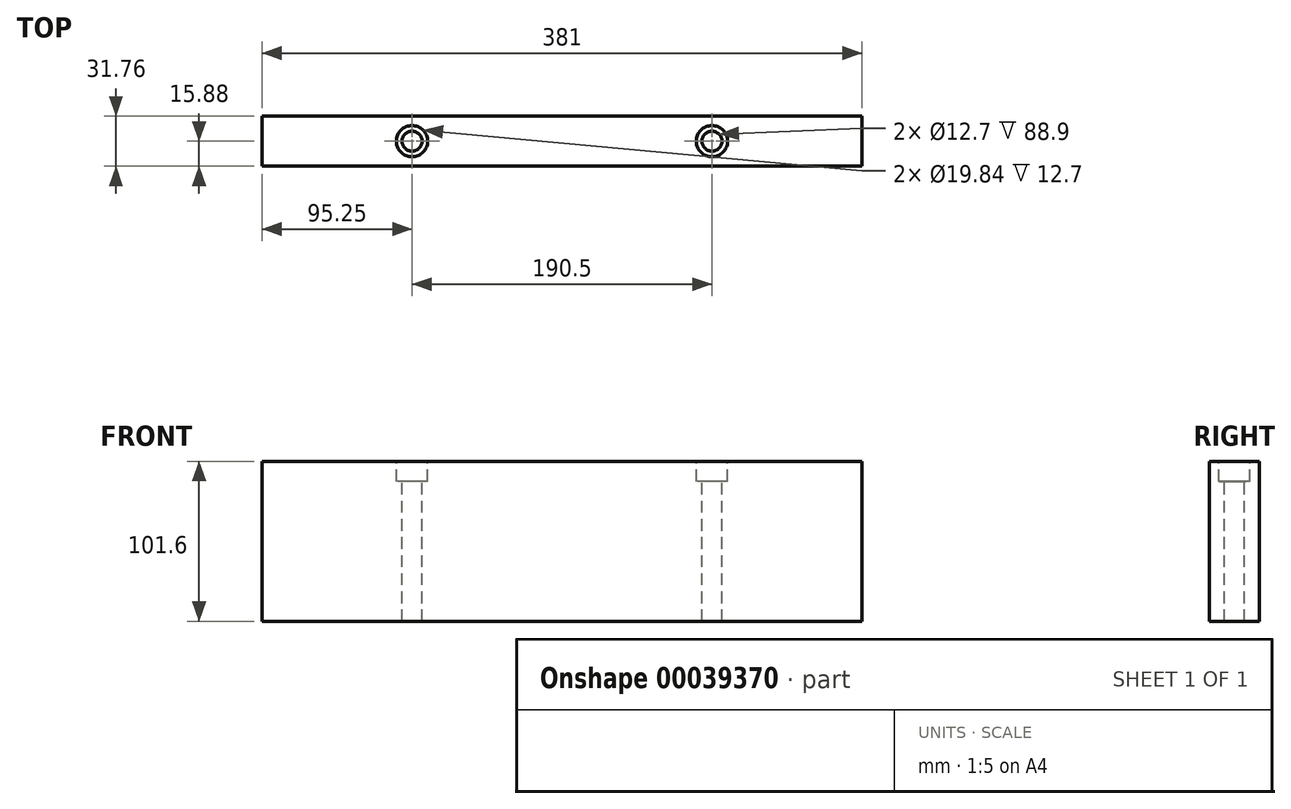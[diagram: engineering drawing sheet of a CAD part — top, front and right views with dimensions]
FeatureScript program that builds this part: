
annotation { "Feature Type Name" : "Feature", "Feature Type Description" : "" }
export const myFeature = defineFeature(function(context is Context, id is Id, definition is map)
    precondition{}
    {
        {
            var Q0;
            Q0=qCreatedBy(makeId("Top.planeOp"),FACE);
            var sketch = newSketch(context, id + "F0", { "sketchPlane" : qUnion([Q0])});
            skLineSegment(sketch, "E0", {"start": v(0, 247.96) * mm, "end": v(0, -242.63) * mm});
            skLineSegment(sketch, "E1", {"start": v(-246.65, 0) * mm, "end": v(251.52, 0) * mm});
            skLineSegment(sketch, "E2.bottom", {"start": v(-190.5, 15.88) * mm, "end": v(190.5, 15.88) * mm});
            skLineSegment(sketch, "E2.top", {"start": v(-190.5, -15.88) * mm, "end": v(190.5, -15.88) * mm});
            skLineSegment(sketch, "E2.left", {"start": v(-190.5, 15.88) * mm, "end": v(-190.5, -15.88) * mm});
            skLineSegment(sketch, "E2.right", {"start": v(190.5, 15.87) * mm, "end": v(190.5, -15.87) * mm});
            skSolve(sketch);
        }
        {
            var Q0;
            Q0 = qSketchRegion(id + "F0", true);
            extrude(context, id + "F1", {"entities" : qUnion([Q0]), "depth" : 101.6 * mm});
        }
        {
            var Q0;
            Q0=makeQuery(id+"F1.opExtrude","CAP_FACE",FACE,{"disambiguationData":[OSD([sQuery(id+"F0.wireOp",EDGE,"E2.bottom"),sQuery(id+"F0.wireOp",EDGE,"E2.top"),sQuery(id+"F0.wireOp",EDGE,"E2.left"),sQuery(id+"F0.wireOp",EDGE,"E2.right")])],"isStart":false});
            var sketch = newSketch(context, id + "F2", { "sketchPlane" : qUnion([Q0])});
            skLineSegment(sketch, "E3", {"start": v(-195.84, 0) * mm, "end": v(195.6, 0) * mm});
            skPoint(sketch, "E3.endSnap0", {"position": v(-190.5, 0) * mm});
            skLineSegment(sketch, "E4", {"start": v(0, 22.9) * mm, "end": v(0, -23.84) * mm});
            skPoint(sketch, "E5", {"position": v(-95.25, 0) * mm});
            skPoint(sketch, "E6", {"position": v(95.25, 0) * mm});
            skSolve(sketch);
        }
        {
            var Q0;
            Q0=sQuery(id+"F2.wireOp",VERTEX,"E5");
            var Q1;
            Q1=sQuery(id+"F2.wireOp",VERTEX,"E6");
            var Q2;
            Q2=makeQuery(id+"F1.opExtrude","SWEPT_BODY",BODY,{"disambiguationData":[OSD([sQuery(id+"F0.wireOp",EDGE,"E2.bottom"),sQuery(id+"F0.wireOp",EDGE,"E2.top"),sQuery(id+"F0.wireOp",EDGE,"E2.left"),sQuery(id+"F0.wireOp",EDGE,"E2.right")])]});
            hole(context, id + "F3", {"style" : HoleStyle.C_BORE, "holeDiameter" : 12.7 * mm, "cBoreDiameter" : 19.84 * mm, "cBoreDepth" : 12.7 * mm, "endStyle" : HoleEndStyle.THROUGH, "locations" : qUnion([Q0, Q1]), "scope" : qUnion([Q2])});
        }
    });
